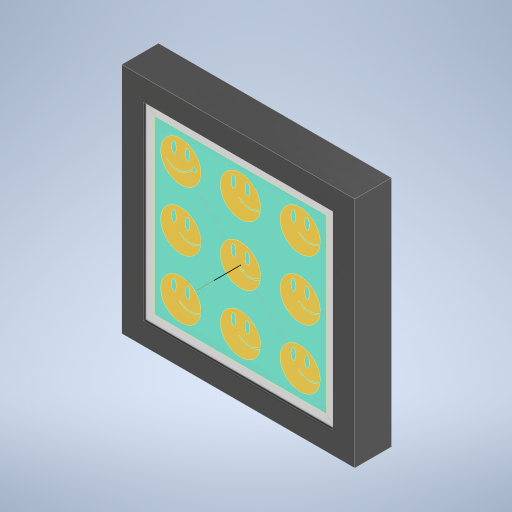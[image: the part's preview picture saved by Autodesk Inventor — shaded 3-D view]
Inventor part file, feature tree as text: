
AUTODESK INVENTOR PART (.ipt)
format: ipt  version: 2023 (Build 270158030, 158C)  size: 738,816 bytes
history: native  units: mm
features: sketch x14, extrude x13, projected_geometry x9, other x7, pattern_circular x1
ambient origin geometry x8: Origin, YZ Plane, XZ Plane, XY Plane, X Axis, Y Axis, Z Axis, Center Point
bodies: Body1 (feature_tree), Body2 (feature_tree), Body3 (feature_tree), Body4 (feature_tree), Body5 (feature_tree)
feature tree (44):
  other  "art"
  extrude  "Extrusion1"  Depth=185.0mm
  extrude  "Extrusion2"  Depth=0.02mm TaperAngle=0.0deg
  extrude  "Extrusion3"  Depth=23.0mm
  extrude  "Extrusion4"  Depth=5.0mm
  extrude  "Extrusion6"  Depth=5.0mm
  extrude  "Extrusion10"  Depth=6.0mm
  extrude  "Extrusion11"  Depth=8.0mm
  extrude  "Extrusion12"  Depth=0.02mm TaperAngle=0.0deg
  extrude  "Extrusion13"  Depth=1.5mm
  sketch  "Sketch21"  dims[d40=25.0mm d41=0.0mm]
  other  "Work Axis1"
  pattern_circular  "Circular Pattern2"  Count=15  [1 undecoded]
  extrude  "Extrusion14"  Depth=17.5mm
  extrude  "Extrusion15"  Depth=17.5mm
  extrude  "Extrusion16"  Depth=200.0mm
  extrude  "Extrusion17"  Depth=200.0mm
  sketch  "Sketch1"  dims[d0=175.0mm d1=185.0mm]
  sketch  "Sketch2"  dims[d2=0.01mm d3=0.0mm d8=0.02mm d9=0.0mm]
  sketch  "Sketch3"  dims[d10=35.0mm d11=23.0mm]
  sketch  "Sketch4"  dims[d12=23.0mm d13=5.0mm]
  other  "back-plate"
  sketch  "Sketch7"  dims[d14=5.0mm d15=2.0mm]
  projected_geometry  "Projected Loop9"
  sketch  "Sketch13"  dims[d16=2.0mm d17=6.0mm]
  projected_geometry  "Projected Loop17"
  sketch  "Sketch15"  dims[d18=6.0mm d19=8.0mm]
  projected_geometry  "Projected Loop18"
  sketch  "Sketch16"  dims[d20=30.0mm d22=52.0mm d23=30.0mm d25=52.0mm d28=0.02mm d29=0.0mm]
  sketch  "Sketch18"  dims[d34=2.0mm d35=0.0mm d39=1.5mm]
  projected_geometry  "Projected Loop19"
  other  "Pattern of back-plate:1"
  other  "back-plate-revolve"
  sketch  "Sketch22"  dims[d42=15.0mm d69=150.0mm]
  projected_geometry  "Projected Loop20"
  projected_geometry  "Projected Loop21"
  other  "closure1"
  sketch  "Sketch23"  dims[d70=150.0mm d71=17.5mm]
  projected_geometry  "Projected Loop22"
  sketch  "Sketch24"  dims[d72=17.5mm d73=12.5mm]
  projected_geometry  "Projected Loop23"
  other  "outer"
  sketch  "Sketch25"  dims[d74=12.5mm d76=200.0mm d77=200.0mm d78=7.5mm d79=7.5mm d80=12.5mm d81=12.5mm d82=15.0mm d83=15.0mm d84=200.0mm d85=55.0mm d86=55.0mm d87=15.0mm d88=40.0mm d90=360.0deg d92=3.0mm d93=0.0mm d101=0.0mm d102=0.0mm d103=15.0mm d104=8.0mm d105=5.0mm d106=13.0mm d107=7.5mm d108=7.5mm d109=2.0mm d110=0.0mm d113=15.0mm d114=7.5mm d115=8.0mm d116=13.0mm d117=8.0mm d118=8.0mm d119=7.5mm d120=8.0mm d121=13.0mm d122=2.0mm d123=0.0mm d130=20.0mm d131=360.0deg d133=10.0mm d134=10.0mm d136=10.0mm d139=1.5mm d140=1.5mm d141=1.5mm d142=1.5mm d143=19.0mm d144=19.0mm d145=19.0mm d146=19.0mm d147=2.0mm d148=0.0mm d149=2.0mm d150=0.0mm d151=1.5mm d152=50.0mm d153=0.0mm d154=15.0mm d155=3.0mm d156=0.0mm]
  projected_geometry  "Projected Loop24"
note: 1 required parameter value undecoded (feature->parameter linkage not recoverable at this tier; creation-order binding heuristic only, values carry confidence <= 0.55)
